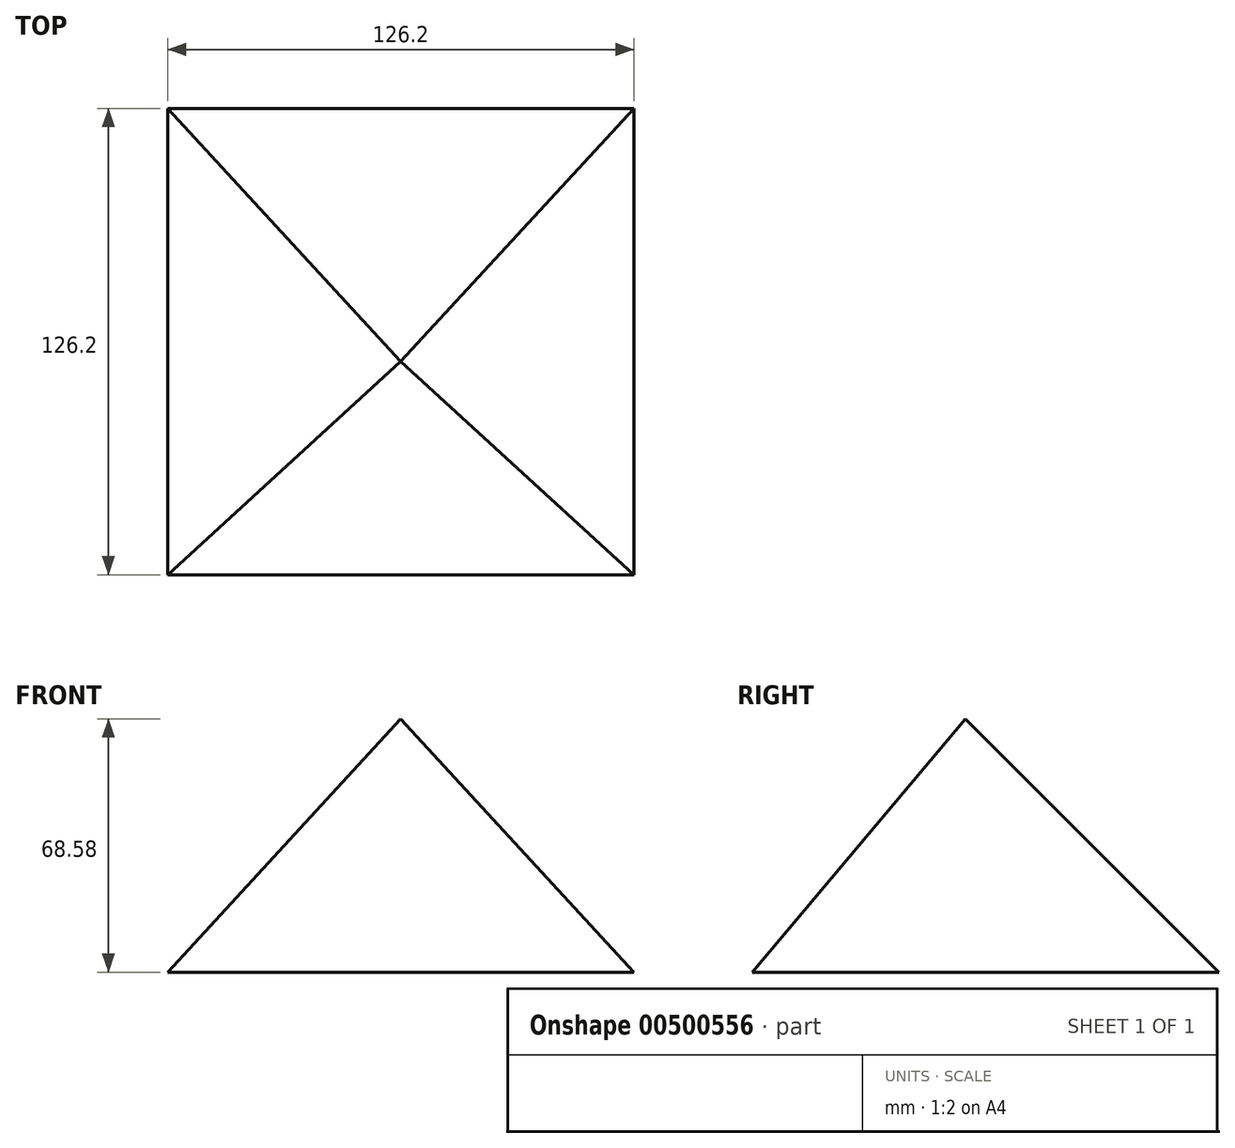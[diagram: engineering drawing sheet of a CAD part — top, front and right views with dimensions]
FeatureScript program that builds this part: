
annotation { "Feature Type Name" : "Feature", "Feature Type Description" : "" }
export const myFeature = defineFeature(function(context is Context, id is Id, definition is map)
    precondition{}
    {
        {
            var Q0;
            Q0=qCreatedBy(makeId("Top.planeOp"),FACE);
            var sketch = newSketch(context, id + "F0", { "sketchPlane" : qUnion([Q0])});
            skCircle(sketch, "E0.cCircle", {"center": v(0, 0) * mm, "radius": 63.1 * mm, "construction": true});
            skLineSegment(sketch, "E0.0", {"start": v(-63.1, 63.1) * mm, "end": v(63.1, 63.1) * mm});
            skLineSegment(sketch, "E0.1", {"start": v(63.1, 63.1) * mm, "end": v(63.1, -63.1) * mm});
            skLineSegment(sketch, "E0.2", {"start": v(63.1, -63.1) * mm, "end": v(-63.1, -63.1) * mm});
            skLineSegment(sketch, "E0.3", {"start": v(-63.1, -63.1) * mm, "end": v(-63.1, 63.1) * mm});
            skPoint(sketch, "E0.0.midPoint", {"position": v(0, 63.1) * mm});
            skSolve(sketch);
        }
        {
            var Q0;
            Q0=qCreatedBy(makeId("Top.planeOp"),FACE);
            cPlane(context, id + "F1", {"entities" : qUnion([Q0]), "cplaneType" : CPlaneType.OFFSET, "offset" : 68.58 * mm, "width" : 152.4 * mm, "height" : 152.4 * mm});
        }
        {
            var Q0;
            Q0=qCreatedBy(id+"F1.planeOp",FACE);
            var sketch = newSketch(context, id + "F2", { "sketchPlane" : qUnion([Q0])});
            skPoint(sketch, "E1", {"position": v(0, -5.43) * mm});
            skSolve(sketch);
        }
        {
            var Q0;
            Q0=sQuery(id+"F2.wireOp",VERTEX,"E1");
            var Q1;
            Q1=makeQuery(id+"F0.imprint","IMPRINT",FACE,{"disambiguationData":[TD([[makeQuery(id+"F0.imprint","IMPRINT",EDGE,{"derivedFrom":sQuery(id+"F0.wireOp",EDGE,"E0.0")}),-1.0]])]});
            loft(context, id + "F3", {"sheetProfilesArray" : [{ "sheetProfileEntities" : qUnion([Q0]) }, { "sheetProfileEntities" : qUnion([Q1]) }]});
        }
    });
